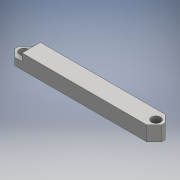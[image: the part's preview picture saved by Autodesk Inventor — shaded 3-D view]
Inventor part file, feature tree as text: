
AUTODESK INVENTOR PART (.ipt)
format: ipt  version: 2016 (Build 200138000, 138)  size: 126,976 bytes
history: native  units: mm
features: extrude x4, chamfer x4, sketch x4, other x1
ambient origin geometry x8: Origin, YZ Plane, XZ Plane, XY Plane, X Axis, Y Axis, Z Axis, Center Point
bodies: Body1 (feature_tree)
feature tree (13):
  other  "ソリッド1"
  extrude  "押し出し1"  Depth=40.0mm
  extrude  "押し出し2"  Depth=4.0mm
  chamfer  "面取り1"  Distance=5.0mm
  chamfer  "面取り2"  Distance=2.5mm
  extrude  "押し出し3"  Depth=2.0mm
  chamfer  "面取り3"  Distance=5.0mm
  chamfer  "面取り4"  Distance=2.0mm Angle=45.0deg
  extrude  "押し出し4"  Depth=2.0mm TaperAngle=45.0deg
  sketch  "スケッチ1"
  sketch  "スケッチ2"
  sketch  "スケッチ3"
  sketch  "スケッチ4"
